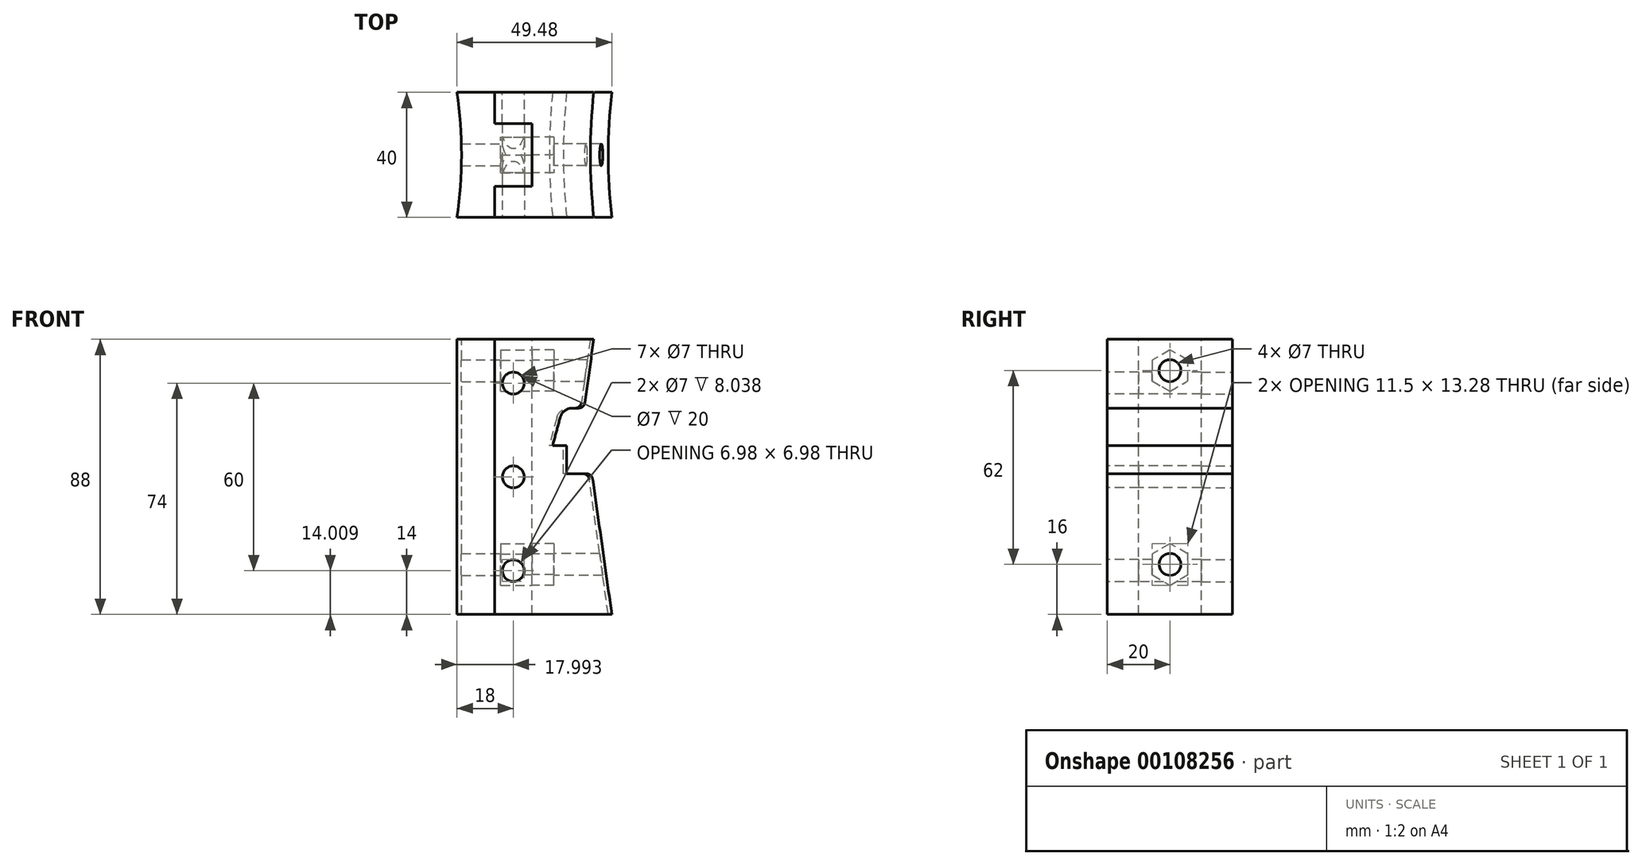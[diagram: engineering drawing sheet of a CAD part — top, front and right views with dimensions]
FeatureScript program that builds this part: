
annotation { "Feature Type Name" : "Feature", "Feature Type Description" : "" }
export const myFeature = defineFeature(function(context is Context, id is Id, definition is map)
    precondition{}
    {
        {
            var Q0;
            Q0=qCreatedBy(makeId("Front.planeOp"),FACE);
            var sketch = newSketch(context, id + "F0", { "sketchPlane" : qUnion([Q0])});
            skLineSegment(sketch, "E0", {"start": v(8.6, 34) * mm, "end": v(5.5, 12) * mm});
            skLineSegment(sketch, "E1", {"start": v(5.5, 12) * mm, "end": v(-1.28, 12) * mm});
            skLineSegment(sketch, "E2", {"start": v(-4.5, 0) * mm, "end": v(0, 0) * mm});
            skLineSegment(sketch, "E3", {"start": v(0, 0) * mm, "end": v(0, -9) * mm});
            skLineSegment(sketch, "E4", {"start": v(0, -9) * mm, "end": v(8, -9) * mm});
            skLineSegment(sketch, "E5", {"start": v(8, -9) * mm, "end": v(14.32, -54) * mm});
            skLineSegment(sketch, "E6", {"start": v(14.32, -54) * mm, "end": v(-15, -54) * mm});
            skLineSegment(sketch, "E7", {"start": v(-15, -54) * mm, "end": v(-15, 34) * mm});
            skLineSegment(sketch, "E8", {"start": v(-15, 34) * mm, "end": v(8.6, 34) * mm});
            skLineSegment(sketch, "E9", {"start": v(187.59, 34) * mm, "end": v(187.59, -54) * mm, "construction": true});
            skLineSegment(sketch, "E10", {"start": v(-4.5, 0) * mm, "end": v(-1.28, 12) * mm});
            skSolve(sketch);
        }
        {
            var Q0;
            Q0 = qSketchRegion(id + "F0", true);
            var Q1;
            Q1=sQuery(id+"F0.wireOp",EDGE,"E9");
            revolve(context, id + "F1", {"entities" : qUnion([Q0]), "axis" : qUnion([Q1]), "revolveType" : RevolveType.SYMMETRIC, "angle" : 30 * degree});
        }
        {
            var Q0;
            Q0=makeQuery(id+"F1.opRevolve","SWEPT_FACE",FACE,{"disambiguationData":[OSD([sQuery(id+"F0.wireOp",EDGE,"E8")])]});
            var sketch = newSketch(context, id + "F2", { "sketchPlane" : qUnion([Q0])});
            skLineSegment(sketch, "E11.bottom", {"start": v(-30, -120) * mm, "end": v(30, -120) * mm});
            skLineSegment(sketch, "E11.top", {"start": v(-10, -20) * mm, "end": v(30, -20) * mm});
            skLineSegment(sketch, "E11.left", {"start": v(-30, -120) * mm, "end": v(-30, -20) * mm});
            skLineSegment(sketch, "E11.right", {"start": v(30, -120) * mm, "end": v(30, -20) * mm});
            skLineSegment(sketch, "E12", {"start": v(0, 0) * mm, "end": v(0, -20) * mm, "construction": true});
            skLineSegment(sketch, "E13", {"start": v(0, 0) * mm, "end": v(-16.63, 0) * mm, "construction": true});
            skLineSegment(sketch, "E14.MirrorCS", {"start": v(-30, 120) * mm, "end": v(30, 120) * mm});
            skLineSegment(sketch, "E15.MirrorCS", {"start": v(-10, 20) * mm, "end": v(30, 20) * mm});
            skLineSegment(sketch, "E16.MirrorCS", {"start": v(30, 120) * mm, "end": v(30, 20) * mm});
            skLineSegment(sketch, "E17.MirrorCS", {"start": v(-30, 120) * mm, "end": v(-30, 20) * mm});
            skLineSegment(sketch, "E18", {"start": v(-10, 20) * mm, "end": v(-10, -20) * mm});
            skLineSegment(sketch, "E19", {"start": v(-30, 20) * mm, "end": v(-30, -20) * mm});
            skSolve(sketch);
        }
        {
            var Q0;
            Q0 = qSketchRegion(id + "F2", true);
            extrude(context, id + "F3", {"entities" : qUnion([Q0]), "operationType" : NewBodyOperationType.REMOVE, "endBound" : BoundingType.THROUGH_ALL, "oppositeDirection" : true, "depth" : 25 * mm});
        }
        {
            var Q0;
            Q0=makeQuery(id+"F1.opRevolve","SWEPT_EDGE",EDGE,{"disambiguationData":[OSD([sQuery(id+"F0.wireOp",EDGE,"E1"),sQuery(id+"F0.wireOp",EDGE,"E10")])]});
            fillet(context, id + "F4", {"entities" : qUnion([Q0]), "radius" : 4 * mm, "tangentPropagation" : true, "allowEdgeOverflow" : false});
        }
        {
            var Q0;
            Q0=makeQuery(id+"F1.opRevolve","SWEPT_EDGE",EDGE,{"disambiguationData":[OSD([sQuery(id+"F0.wireOp",EDGE,"E0"),sQuery(id+"F0.wireOp",EDGE,"E1")])]});
            var Q1;
            Q1=makeQuery(id+"F1.opRevolve","SWEPT_EDGE",EDGE,{"disambiguationData":[OSD([sQuery(id+"F0.wireOp",EDGE,"E4"),sQuery(id+"F0.wireOp",EDGE,"E5")])]});
            fillet(context, id + "F5", {"entities" : qUnion([Q0, Q1]), "radius" : 2 * mm, "tangentPropagation" : true, "allowEdgeOverflow" : false});
        }
        {
            var Q0;
            Q0=makeQuery(id+"F3.boolean.opBoolean","COPY",FACE,{"derivedFrom":makeQuery(id+"F3.opExtrude","SWEPT_FACE",FACE,{"disambiguationData":[OSD([sQuery(id+"F2.wireOp",EDGE,"E18")])]})});
            var sketch = newSketch(context, id + "F6", { "sketchPlane" : qUnion([Q0])});
            skCircle(sketch, "E20.cCircle", {"center": v(0, 24) * mm, "radius": 5.75 * mm, "construction": true});
            skLineSegment(sketch, "E20.0", {"start": v(0, 30.64) * mm, "end": v(5.75, 27.32) * mm});
            skLineSegment(sketch, "E20.1", {"start": v(5.75, 27.32) * mm, "end": v(5.75, 20.68) * mm});
            skLineSegment(sketch, "E20.2", {"start": v(5.75, 20.68) * mm, "end": v(0, 17.36) * mm});
            skLineSegment(sketch, "E20.3", {"start": v(0, 17.36) * mm, "end": v(-5.75, 20.68) * mm});
            skLineSegment(sketch, "E20.4", {"start": v(-5.75, 20.68) * mm, "end": v(-5.75, 27.32) * mm});
            skLineSegment(sketch, "E20.5", {"start": v(-5.75, 27.32) * mm, "end": v(0, 30.64) * mm});
            skPoint(sketch, "E20.0.midPoint", {"position": v(2.88, 28.98) * mm});
            skCircle(sketch, "E21.cCircle", {"center": v(0, -38) * mm, "radius": 5.75 * mm, "construction": true});
            skLineSegment(sketch, "E21.0", {"start": v(0, -31.36) * mm, "end": v(5.75, -34.68) * mm});
            skLineSegment(sketch, "E21.1", {"start": v(5.75, -34.68) * mm, "end": v(5.75, -41.32) * mm});
            skLineSegment(sketch, "E21.2", {"start": v(5.75, -41.32) * mm, "end": v(0, -44.64) * mm});
            skLineSegment(sketch, "E21.3", {"start": v(0, -44.64) * mm, "end": v(-5.75, -41.32) * mm});
            skLineSegment(sketch, "E21.4", {"start": v(-5.75, -41.32) * mm, "end": v(-5.75, -34.68) * mm});
            skLineSegment(sketch, "E21.5", {"start": v(-5.75, -34.68) * mm, "end": v(0, -31.36) * mm});
            skPoint(sketch, "E21.0.midPoint", {"position": v(2.88, -33.02) * mm});
            skLineSegment(sketch, "E22", {"start": v(0, 24) * mm, "end": v(0, 0) * mm, "construction": true});
            skLineSegment(sketch, "E23", {"start": v(0, 0) * mm, "end": v(0, -38) * mm, "construction": true});
            skCircle(sketch, "E24", {"center": v(0, 24) * mm, "radius": 3.5 * mm});
            skCircle(sketch, "E25", {"center": v(0, -38) * mm, "radius": 3.5 * mm});
            skSolve(sketch);
        }
        {
            var Q0;
            Q0 = qSketchRegion(id + "F6", true);
            var Q1;
            Q1=makeQuery(id+"F6.imprint","IMPRINT",FACE,{"disambiguationData":[TD([[makeQuery(id+"F6.imprint","IMPRINT",EDGE,{"derivedFrom":sQuery(id+"F6.wireOp",EDGE,"E24")}),1.0]])]});
            var Q2;
            Q2=makeQuery(id+"F6.imprint","IMPRINT",FACE,{"disambiguationData":[TD([[makeQuery(id+"F6.imprint","IMPRINT",EDGE,{"derivedFrom":sQuery(id+"F6.wireOp",EDGE,"E25")}),1.0]])]});
            extrude(context, id + "F7", {"entities" : qUnion([Q0, Q1, Q2]), "operationType" : NewBodyOperationType.REMOVE, "oppositeDirection" : true, "depth" : 7 * mm});
        }
        {
            var Q0;
            Q0=makeQuery(id+"F6.imprint","IMPRINT",FACE,{"disambiguationData":[TD([[makeQuery(id+"F6.imprint","IMPRINT",EDGE,{"derivedFrom":sQuery(id+"F6.wireOp",EDGE,"E24")}),1.0]])]});
            var Q1;
            Q1=makeQuery(id+"F6.imprint","IMPRINT",FACE,{"disambiguationData":[TD([[makeQuery(id+"F6.imprint","IMPRINT",EDGE,{"derivedFrom":sQuery(id+"F6.wireOp",EDGE,"E25")}),1.0]])]});
            extrude(context, id + "F8", {"entities" : qUnion([Q0, Q1]), "operationType" : NewBodyOperationType.REMOVE, "endBound" : BoundingType.THROUGH_ALL, "oppositeDirection" : true, "depth" : 25 * mm});
        }
        {
            var Q0;
            Q0=makeQuery(id+"F3.boolean.opBoolean","COPY",FACE,{"derivedFrom":makeQuery(id+"F3.opExtrude","SWEPT_FACE",FACE,{"disambiguationData":[OSD([sQuery(id+"F2.wireOp",EDGE,"E11.top")])]})});
            var sketch = newSketch(context, id + "F9", { "sketchPlane" : qUnion([Q0])});
            skLineSegment(sketch, "E26", {"start": v(-10, 34) * mm, "end": v(-22, 34) * mm});
            skLineSegment(sketch, "E27", {"start": v(-22, 34) * mm, "end": v(-22, -54) * mm});
            skLineSegment(sketch, "E28", {"start": v(-22, -54) * mm, "end": v(-10, -54) * mm});
            skLineSegment(sketch, "E29", {"start": v(-10, -54) * mm, "end": v(-10, 34) * mm});
            skLineSegment(sketch, "E30", {"start": v(-16, 34) * mm, "end": v(-16, 20) * mm, "construction": true});
            skLineSegment(sketch, "E31", {"start": v(-16, 20) * mm, "end": v(-16, -10) * mm, "construction": true});
            skLineSegment(sketch, "E32", {"start": v(-16, -10) * mm, "end": v(-16, -40) * mm, "construction": true});
            skLineSegment(sketch, "E33", {"start": v(-16, -40) * mm, "end": v(-16, -54) * mm, "construction": true});
            skCircle(sketch, "E34", {"center": v(-16, 20) * mm, "radius": 3.5 * mm});
            skCircle(sketch, "E35", {"center": v(-16, -10) * mm, "radius": 3.5 * mm});
            skCircle(sketch, "E36", {"center": v(-16, -40) * mm, "radius": 3.5 * mm});
            skSolve(sketch);
        }
        {
            var Q0;
            Q0 = qSketchRegion(id + "F9", true);
            extrude(context, id + "F10", {"entities" : qUnion([Q0]), "oppositeDirection" : true, "depth" : 10 * mm});
        }
        {
            var Q0;
            Q0=makeQuery(id+"F10.opExtrude","SWEPT_BODY",BODY,{"disambiguationData":[OSD([sQuery(id+"F9.wireOp",EDGE,"E26"),sQuery(id+"F9.wireOp",EDGE,"E27"),sQuery(id+"F9.wireOp",EDGE,"E28"),sQuery(id+"F9.wireOp",EDGE,"E29"),sQuery(id+"F9.wireOp",EDGE,"E34"),sQuery(id+"F9.wireOp",EDGE,"E35"),sQuery(id+"F9.wireOp",EDGE,"E36")])]});
            var Q1;
            Q1=qCreatedBy(makeId("Front.planeOp"),FACE);
            mirror(context, id + "F11", {"entities" : qUnion([Q0]), "mirrorPlane" : qUnion([Q1])});
        }
        {
            var Q0;
            Q0=makeQuery(id+"F1.opRevolve","SWEPT_BODY",BODY,{"disambiguationData":[OSD([sQuery(id+"F0.wireOp",EDGE,"E0"),sQuery(id+"F0.wireOp",EDGE,"E1"),sQuery(id+"F0.wireOp",EDGE,"E2"),sQuery(id+"F0.wireOp",EDGE,"E3"),sQuery(id+"F0.wireOp",EDGE,"E4"),sQuery(id+"F0.wireOp",EDGE,"E5"),sQuery(id+"F0.wireOp",EDGE,"E6"),sQuery(id+"F0.wireOp",EDGE,"E7"),sQuery(id+"F0.wireOp",EDGE,"E8"),sQuery(id+"F0.wireOp",EDGE,"E10")])]});
            var Q1;
            Q1=makeQuery(id+"F10.opExtrude","SWEPT_BODY",BODY,{"disambiguationData":[OSD([sQuery(id+"F9.wireOp",EDGE,"E26"),sQuery(id+"F9.wireOp",EDGE,"E27"),sQuery(id+"F9.wireOp",EDGE,"E28"),sQuery(id+"F9.wireOp",EDGE,"E29"),sQuery(id+"F9.wireOp",EDGE,"E34"),sQuery(id+"F9.wireOp",EDGE,"E35"),sQuery(id+"F9.wireOp",EDGE,"E36")])]});
            var Q2;
            Q2=makeQuery(id+"F11.opPattern","COPY",BODY,{"derivedFrom":makeQuery(id+"F10.opExtrude","SWEPT_BODY",BODY,{"disambiguationData":[OSD([sQuery(id+"F9.wireOp",EDGE,"E26"),sQuery(id+"F9.wireOp",EDGE,"E27"),sQuery(id+"F9.wireOp",EDGE,"E28"),sQuery(id+"F9.wireOp",EDGE,"E29"),sQuery(id+"F9.wireOp",EDGE,"E34"),sQuery(id+"F9.wireOp",EDGE,"E35"),sQuery(id+"F9.wireOp",EDGE,"E36")])]}),"instanceName":"1"});
            booleanBodies(context, id + "F12", {"operationType" : BooleanOperationType.UNION, "tools" : qUnion([Q0, Q1, Q2])});
        }
        {
            var Q0;
            {var subQ0=makeQuery(id+"F10.opExtrude","SWEPT_FACE",FACE,{"disambiguationData":[OSD([sQuery(id+"F9.wireOp",EDGE,"E26")])]});Q0=makeQuery(id+"F12.opBoolean","MERGE",FACE,{"derivedFrom":[makeQuery(id+"F1.opRevolve","SWEPT_FACE",FACE,{"disambiguationData":[OSD([sQuery(id+"F0.wireOp",EDGE,"E8")])]}),subQ0,makeQuery(id+"F11.opPattern","COPY",FACE,{"derivedFrom":subQ0,"instanceName":"1"})]});}
            var sketch = newSketch(context, id + "F13", { "sketchPlane" : qUnion([Q0])});
            skLineSegment(sketch, "E37.0", {"start": v(-22, 10) * mm, "end": v(-22, 20) * mm});
            skLineSegment(sketch, "E37.1", {"start": v(-10, 10) * mm, "end": v(-22, 10) * mm});
            skLineSegment(sketch, "E37.2", {"start": v(-10, 10) * mm, "end": v(-10, -10) * mm});
            skLineSegment(sketch, "E37.3", {"start": v(-10, -10) * mm, "end": v(-22, -10) * mm});
            skLineSegment(sketch, "E37.4", {"start": v(-22, -10) * mm, "end": v(-22, -20) * mm});
            skLineSegment(sketch, "E38", {"start": v(-22, 20) * mm, "end": v(-34, 20) * mm});
            skLineSegment(sketch, "E39", {"start": v(-22, -20) * mm, "end": v(-34, -20) * mm});
            skArc(sketch, "E40", {"start": v(-34, -20) * mm, "mid": v(-32.56, 0) * mm, "end": v(-34, 20) * mm});
            skSolve(sketch);
        }
        {
            var Q0;
            Q0 = qSketchRegion(id + "F13", true);
            var Q1;
            {var subQ0=makeQuery(id+"F10.opExtrude","SWEPT_FACE",FACE,{"disambiguationData":[OSD([sQuery(id+"F9.wireOp",EDGE,"E28")])]});Q1=makeQuery(id+"F12.opBoolean","MERGE",FACE,{"derivedFrom":[makeQuery(id+"F1.opRevolve","SWEPT_FACE",FACE,{"disambiguationData":[OSD([sQuery(id+"F0.wireOp",EDGE,"E6")])]}),subQ0,makeQuery(id+"F11.opPattern","COPY",FACE,{"derivedFrom":subQ0,"instanceName":"1"})]});}
            extrude(context, id + "F14", {"entities" : qUnion([Q0]), "endBound" : BoundingType.UP_TO_SURFACE, "oppositeDirection" : true, "endBoundEntityFace" : qUnion([Q1]), "depth" : 25 * mm});
        }
        {
            var Q0;
            Q0=makeQuery(id+"F9.imprint","IMPRINT",FACE,{"disambiguationData":[TD([[makeQuery(id+"F9.imprint","IMPRINT",EDGE,{"derivedFrom":sQuery(id+"F9.wireOp",EDGE,"E34")}),1.0]])]});
            var Q1;
            Q1=makeQuery(id+"F9.imprint","IMPRINT",FACE,{"disambiguationData":[TD([[makeQuery(id+"F9.imprint","IMPRINT",EDGE,{"derivedFrom":sQuery(id+"F9.wireOp",EDGE,"E35")}),1.0]])]});
            var Q2;
            Q2=makeQuery(id+"F9.imprint","IMPRINT",FACE,{"disambiguationData":[TD([[makeQuery(id+"F9.imprint","IMPRINT",EDGE,{"derivedFrom":sQuery(id+"F9.wireOp",EDGE,"E36")}),1.0]])]});
            extrude(context, id + "F15", {"entities" : qUnion([Q0, Q1, Q2]), "operationType" : NewBodyOperationType.REMOVE, "endBound" : BoundingType.THROUGH_ALL, "oppositeDirection" : true, "depth" : 25 * mm});
        }
        {
            var Q0;
            Q0=makeQuery(id+"F6.imprint","IMPRINT",FACE,{"disambiguationData":[TD([[makeQuery(id+"F6.imprint","IMPRINT",EDGE,{"derivedFrom":sQuery(id+"F6.wireOp",EDGE,"E25")}),1.0]])]});
            var Q1;
            Q1=makeQuery(id+"F6.imprint","IMPRINT",FACE,{"disambiguationData":[TD([[makeQuery(id+"F6.imprint","IMPRINT",EDGE,{"derivedFrom":sQuery(id+"F6.wireOp",EDGE,"E24")}),1.0]])]});
            extrude(context, id + "F16", {"entities" : qUnion([Q0, Q1]), "operationType" : NewBodyOperationType.REMOVE, "endBound" : BoundingType.THROUGH_ALL, "depth" : 25 * mm});
        }
        {
            var Q0;
            Q0=makeQuery(id+"F6.imprint","IMPRINT",FACE,{"disambiguationData":[TD([[makeQuery(id+"F6.imprint","IMPRINT",EDGE,{"derivedFrom":sQuery(id+"F6.wireOp",EDGE,"E21.0")}),-1.0]])]});
            var Q1;
            Q1=makeQuery(id+"F6.imprint","IMPRINT",FACE,{"disambiguationData":[TD([[makeQuery(id+"F6.imprint","IMPRINT",EDGE,{"derivedFrom":sQuery(id+"F6.wireOp",EDGE,"E20.0")}),-1.0]])]});
            extrude(context, id + "F17", {"entities" : qUnion([Q0, Q1]), "operationType" : NewBodyOperationType.REMOVE, "depth" : 10 * mm});
        }
    });
